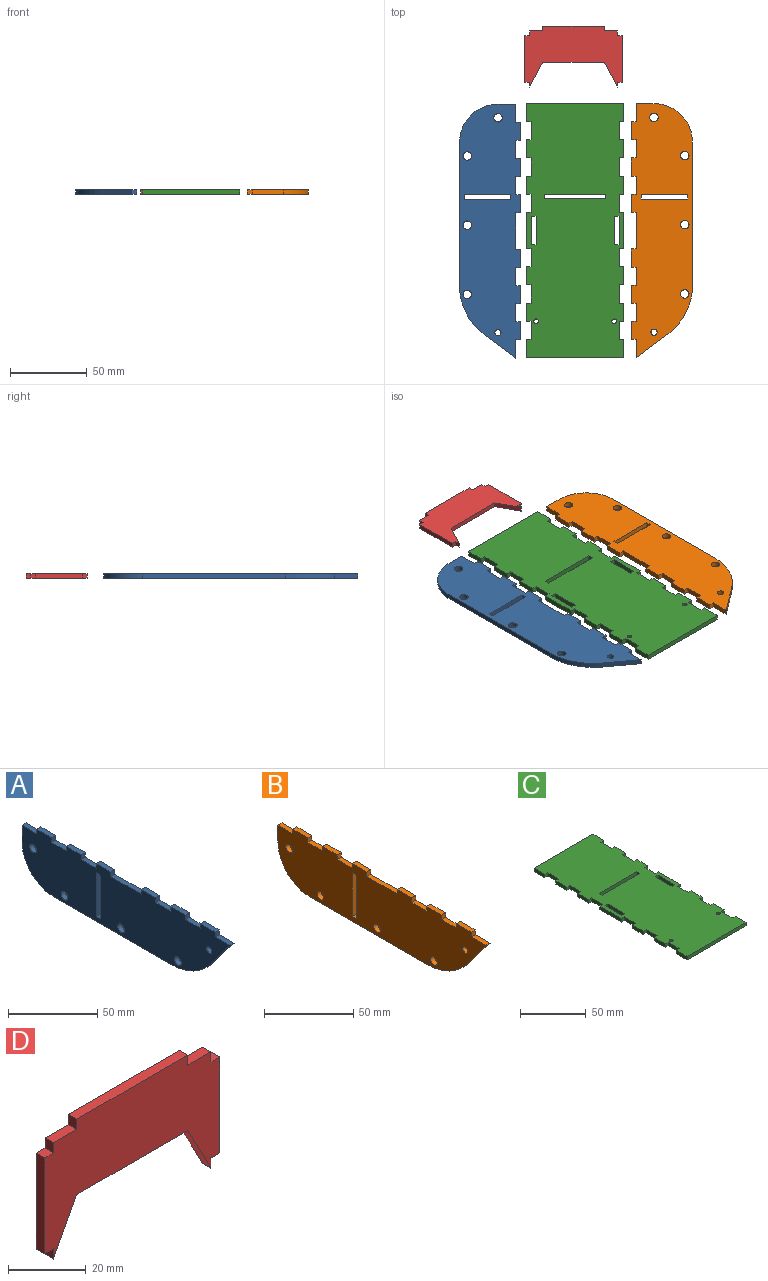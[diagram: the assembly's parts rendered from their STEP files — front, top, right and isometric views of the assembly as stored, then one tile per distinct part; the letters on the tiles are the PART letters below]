
ASSEMBLY  parts=4 mates=3
PART A: 41 faces, bbox 3.2x165.1x39.7 mm
  f0: plane 165.1x39.68mm, normal (-1,0,0), area 5359.6mm2, adj f1,f2,f3,f4,f5,f6,f7,f8
  f1: plane 11.79x3.18mm, normal (0,0,1), area 37.4mm2, adj f0,f2,f28,f29
  f2: plane 3.18x3.18mm, normal (0,-1,0), area 10.1mm2, adj f0,f1,f3,f29
  f3: plane 11.72x3.18mm, normal (0,0,1), area 37.2mm2, adj f0,f2,f4,f29
  f4: plane 3.18x3.18mm, normal (0,1,0), area 10.1mm2, adj f0,f3,f5,f29
  f5: plane 11.79x3.18mm, normal (0,0,1), area 37.4mm2, adj f0,f4,f6,f29
  f6: plane 3.18x3.18mm, normal (0,-1,0), area 10.1mm2, adj f0,f5,f7,f29
  f7: plane 11.72x3.18mm, normal (0,0,1), area 37.2mm2, adj f0,f6,f8,f29
  f8: plane 3.18x3.18mm, normal (0,1,0), area 10.1mm2, adj f0,f7,f9,f29
  f9: plane 11.79x3.18mm, normal (0,0,1), area 37.4mm2, adj f0,f8,f10,f29
  f10: plane 3.18x3.18mm, normal (0,-1,0), area 10.1mm2, adj f0,f9,f11,f29
  f11: plane 11.79x3.18mm, normal (0,0,1), area 37.4mm2, adj f0,f10,f12,f29
  f12: plane 20.51x15.27mm, normal (0,-0.8,-0.6), area 81.2mm2, adj f0,f11,f13,f29
  f13: cylinder r=39.68mm len=31.83mm, axis (1,0,0), area 117.3mm2, adj f0,f12,f14,f29
  f14: plane 93x3.18mm, normal (0,0,-1), area 295.3mm2, adj f0,f13,f15,f29
  f15: cylinder r=25mm len=25mm, axis (1,0,0), area 124.7mm2, adj f0,f14,f16,f29
  f16: plane 11.5x3.18mm, normal (0,1,0), area 36.5mm2, adj f0,f15,f17,f29
  f17: plane 11.79x3.18mm, normal (0,0,1), area 37.4mm2, adj f0,f16,f18,f29
  f18: plane 3.18x3.18mm, normal (0,1,0), area 10.1mm2, adj f0,f17,f19,f29
  f19: plane 11.79x3.18mm, normal (0,0,1), area 37.4mm2, adj f0,f18,f20,f29
  f20: plane 3.18x3.18mm, normal (0,-1,0), area 10.1mm2, adj f0,f19,f21,f29
  f21: plane 11.72x3.18mm, normal (0,0,1), area 37.2mm2, adj f0,f20,f22,f29
  f22: plane 3.18x3.18mm, normal (0,1,0), area 10.1mm2, adj f0,f21,f23,f29
  f23: plane 11.79x3.18mm, normal (0,0,1), area 37.4mm2, adj f0,f22,f24,f29
  f24: plane 3.18x3.18mm, normal (0,-1,0), area 10.1mm2, adj f0,f23,f25,f29
  f25: plane 11.72x3.18mm, normal (0,0,1), area 37.2mm2, adj f0,f24,f26,f29
  f26: plane 3.18x3.18mm, normal (0,1,0), area 10.1mm2, adj f0,f25,f27,f29
  f27: plane 11.79x3.18mm, normal (0,0,1), area 37.4mm2, adj f0,f26,f29,f31
  f28: plane 3.18x3.18mm, normal (0,1,0), area 10.1mm2, adj f0,f1,f29,f32
  f29: plane 165.1x39.68mm, normal (1,0,0), area 5359.6mm2, adj f1,f2,f3,f4,f5,f6,f7,f8
  f30: cylinder r=2.75mm len=5.5mm, axis (1,0,0), area 54.9mm2, adj f0,f29
  f31: plane 3.18x3.18mm, normal (0,-1,0), area 10.1mm2, adj f0,f27,f29,f32
  f32: plane 23.89x3.18mm, normal (0,0,1), area 75.8mm2, adj f0,f28,f29,f31
  f33: cylinder r=2.75mm len=5.5mm, axis (1,0,0), area 54.9mm2, adj f0,f29
  f34: cylinder r=2mm len=4mm, axis (1,0,0), area 39.9mm2, adj f0,f29
  f35: cylinder r=2.75mm len=5.5mm, axis (1,0,0), area 54.9mm2, adj f0,f29
  f36: cylinder r=2.75mm len=5.5mm, axis (1,0,0), area 54.9mm2, adj f0,f29
  f37: plane 30.15x3.18mm, normal (0,1,0), area 95.7mm2, adj f0,f29,f39,f40
  f38: plane 30.15x3.18mm, normal (0,-1,0), area 95.7mm2, adj f0,f29,f39,f40
  f39: plane 3.18x3.18mm, normal (0,0,-1), area 10.1mm2, adj f0,f29,f37,f38
  f40: plane 3.18x3.18mm, normal (0,0,1), area 10.1mm2, adj f0,f29,f37,f38
PART B: 41 faces, bbox 3.2x165.1x39.7 mm
  f0: plane 165.1x39.68mm, normal (1,0,0), area 5359.6mm2, adj f2,f3,f4,f5,f6,f7,f8,f9
  f1: plane 165.1x39.68mm, normal (-1,0,0), area 5359.6mm2, adj f2,f3,f4,f5,f6,f7,f8,f9
  f2: plane 11.79x3.18mm, normal (0,0,1), area 37.4mm2, adj f0,f1,f3,f29
  f3: plane 3.18x3.18mm, normal (0,-1,0), area 10.1mm2, adj f0,f1,f2,f4
  f4: plane 11.72x3.18mm, normal (0,0,1), area 37.2mm2, adj f0,f1,f3,f5
  f5: plane 3.18x3.18mm, normal (0,1,0), area 10.1mm2, adj f0,f1,f4,f6
  f6: plane 11.79x3.18mm, normal (0,0,1), area 37.4mm2, adj f0,f1,f5,f7
  f7: plane 3.18x3.18mm, normal (0,-1,0), area 10.1mm2, adj f0,f1,f6,f8
  f8: plane 11.72x3.18mm, normal (0,0,1), area 37.2mm2, adj f0,f1,f7,f9
  f9: plane 3.18x3.18mm, normal (0,1,0), area 10.1mm2, adj f0,f1,f8,f10
  f10: plane 11.79x3.18mm, normal (0,0,1), area 37.4mm2, adj f0,f1,f9,f11
  f11: plane 3.18x3.18mm, normal (0,-1,0), area 10.1mm2, adj f0,f1,f10,f12
  f12: plane 11.79x3.18mm, normal (0,0,1), area 37.4mm2, adj f0,f1,f11,f13
  f13: plane 20.51x15.27mm, normal (0,-0.8,-0.6), area 81.2mm2, adj f0,f1,f12,f14
  f14: cylinder r=39.68mm len=31.83mm, axis (-1,0,0), area 117.3mm2, adj f0,f1,f13,f15
  f15: plane 93x3.18mm, normal (0,0,-1), area 295.3mm2, adj f0,f1,f14,f16
  f16: cylinder r=25mm len=25mm, axis (-1,0,0), area 124.7mm2, adj f0,f1,f15,f17
  f17: plane 11.5x3.18mm, normal (0,1,0), area 36.5mm2, adj f0,f1,f16,f18
  f18: plane 11.79x3.18mm, normal (0,0,1), area 37.4mm2, adj f0,f1,f17,f19
  f19: plane 3.18x3.18mm, normal (0,1,0), area 10.1mm2, adj f0,f1,f18,f20
  f20: plane 11.79x3.18mm, normal (0,0,1), area 37.4mm2, adj f0,f1,f19,f21
  f21: plane 3.18x3.18mm, normal (0,-1,0), area 10.1mm2, adj f0,f1,f20,f22
  f22: plane 11.72x3.18mm, normal (0,0,1), area 37.2mm2, adj f0,f1,f21,f23
  f23: plane 3.18x3.18mm, normal (0,1,0), area 10.1mm2, adj f0,f1,f22,f24
  f24: plane 11.79x3.18mm, normal (0,0,1), area 37.4mm2, adj f0,f1,f23,f25
  f25: plane 3.18x3.18mm, normal (0,-1,0), area 10.1mm2, adj f0,f1,f24,f26
  f26: plane 11.72x3.18mm, normal (0,0,1), area 37.2mm2, adj f0,f1,f25,f27
  f27: plane 3.18x3.18mm, normal (0,1,0), area 10.1mm2, adj f0,f1,f26,f28
  f28: plane 11.79x3.18mm, normal (0,0,1), area 37.4mm2, adj f0,f1,f27,f31
  f29: plane 3.18x3.18mm, normal (0,1,0), area 10.1mm2, adj f0,f1,f2,f32
  f30: cylinder r=2.75mm len=5.5mm, axis (-1,0,0), area 54.9mm2, adj f0,f1
  f31: plane 3.18x3.18mm, normal (0,-1,0), area 10.1mm2, adj f0,f1,f28,f32
  f32: plane 23.89x3.18mm, normal (0,0,1), area 75.8mm2, adj f0,f1,f29,f31
  f33: cylinder r=2.75mm len=5.5mm, axis (-1,0,0), area 54.9mm2, adj f0,f1
  f34: cylinder r=2mm len=4mm, axis (-1,0,0), area 39.9mm2, adj f0,f1
  f35: cylinder r=2.75mm len=5.5mm, axis (-1,0,0), area 54.9mm2, adj f0,f1
  f36: cylinder r=2.75mm len=5.5mm, axis (-1,0,0), area 54.9mm2, adj f0,f1
  f37: plane 30.15x3.18mm, normal (0,1,0), area 95.7mm2, adj f0,f1,f39,f40
  f38: plane 30.15x3.18mm, normal (0,-1,0), area 95.7mm2, adj f0,f1,f39,f40
  f39: plane 3.18x3.18mm, normal (0,0,-1), area 10.1mm2, adj f0,f1,f37,f38
  f40: plane 3.18x3.18mm, normal (0,0,1), area 10.1mm2, adj f0,f1,f37,f38
PART C: 68 faces, bbox 63.5x165.1x3.2 mm
  f0: plane 165.1x63.5mm, normal (0,0,1), area 9776.6mm2, adj f2,f3,f4,f5,f6,f7,f8,f9
  f1: plane 165.1x63.5mm, normal (0,0,-1), area 9776.6mm2, adj f2,f3,f4,f5,f6,f7,f8,f9
  f2: plane 11.79x3.18mm, normal (-1,0,0), area 37.4mm2, adj f0,f1,f3,f60
  f3: plane 63.5x3.18mm, normal (0,-1,0), area 201.6mm2, adj f0,f1,f2,f4
  f4: plane 11.79x3.18mm, normal (1,0,0), area 37.4mm2, adj f0,f1,f3,f5
  f5: plane 3.18x3.18mm, normal (0,1,0), area 10.1mm2, adj f0,f1,f4,f6
  f6: plane 11.79x3.18mm, normal (1,0,0), area 37.4mm2, adj f0,f1,f5,f7
  f7: plane 3.18x3.18mm, normal (0,-1,0), area 10.1mm2, adj f0,f1,f6,f8
  f8: plane 11.79x3.18mm, normal (1,0,0), area 37.4mm2, adj f0,f1,f7,f9
  f9: plane 3.18x3.18mm, normal (0,1,0), area 10.1mm2, adj f0,f1,f8,f10
  f10: plane 11.79x3.18mm, normal (1,0,0), area 37.4mm2, adj f0,f1,f9,f11
  f11: plane 3.18x3.18mm, normal (0,-1,0), area 10.1mm2, adj f0,f1,f10,f12
  f12: plane 11.79x3.18mm, normal (1,0,0), area 37.4mm2, adj f0,f1,f11,f13
  f13: plane 3.18x3.18mm, normal (0,1,0), area 10.1mm2, adj f0,f1,f12,f14
  f14: plane 11.79x3.18mm, normal (1,0,0), area 37.4mm2, adj f0,f1,f13,f15
  f15: plane 3.18x3.18mm, normal (0,-1,0), area 10.1mm2, adj f0,f1,f14,f16
  f16: plane 23.59x3.18mm, normal (1,0,0), area 74.9mm2, adj f0,f1,f15,f17
  f17: plane 3.18x3.18mm, normal (0,1,0), area 10.1mm2, adj f0,f1,f16,f18
  f18: plane 11.79x3.18mm, normal (1,0,0), area 37.4mm2, adj f0,f1,f17,f19
  f19: plane 3.18x3.18mm, normal (0,-1,0), area 10.1mm2, adj f0,f1,f18,f20
  f20: plane 11.79x3.18mm, normal (1,0,0), area 37.4mm2, adj f0,f1,f19,f21
  f21: plane 3.18x3.18mm, normal (0,1,0), area 10.1mm2, adj f0,f1,f20,f22
  f22: plane 11.79x3.18mm, normal (1,0,0), area 37.4mm2, adj f0,f1,f21,f23
  f23: plane 3.18x3.18mm, normal (0,-1,0), area 10.1mm2, adj f0,f1,f22,f24
  f24: plane 11.79x3.18mm, normal (1,0,0), area 37.4mm2, adj f0,f1,f23,f25
  f25: plane 3.18x3.18mm, normal (0,1,0), area 10.1mm2, adj f0,f1,f24,f26
  f26: plane 11.79x3.18mm, normal (1,0,0), area 37.4mm2, adj f0,f1,f25,f27
  f27: plane 3.18x3.18mm, normal (0,-1,0), area 10.1mm2, adj f0,f1,f26,f28
  f28: plane 11.79x3.18mm, normal (1,0,0), area 37.4mm2, adj f0,f1,f27,f29
  f29: plane 63.5x3.18mm, normal (0,1,0), area 201.6mm2, adj f0,f1,f28,f30
  f30: plane 11.79x3.18mm, normal (-1,0,0), area 37.4mm2, adj f0,f1,f29,f31
  f31: plane 3.18x3.18mm, normal (0,-1,0), area 10.1mm2, adj f0,f1,f30,f32
  f32: plane 11.79x3.18mm, normal (-1,0,0), area 37.4mm2, adj f0,f1,f31,f33
  f33: plane 3.18x3.18mm, normal (0,1,0), area 10.1mm2, adj f0,f1,f32,f34
  f34: plane 11.79x3.18mm, normal (-1,0,0), area 37.4mm2, adj f0,f1,f33,f35
  f35: plane 3.18x3.18mm, normal (0,-1,0), area 10.1mm2, adj f0,f1,f34,f36
  f36: plane 11.79x3.18mm, normal (-1,0,0), area 37.4mm2, adj f0,f1,f35,f37
  f37: plane 3.18x3.18mm, normal (0,1,0), area 10.1mm2, adj f0,f1,f36,f38
  f38: plane 11.79x3.18mm, normal (-1,0,0), area 37.4mm2, adj f0,f1,f37,f39
  f39: plane 3.18x3.18mm, normal (0,-1,0), area 10.1mm2, adj f0,f1,f38,f40
  f40: plane 11.79x3.18mm, normal (-1,0,0), area 37.4mm2, adj f0,f1,f39,f41
  f41: plane 3.18x3.18mm, normal (0,1,0), area 10.1mm2, adj f0,f1,f40,f42
  f42: plane 23.59x3.18mm, normal (-1,0,0), area 74.9mm2, adj f0,f1,f41,f43
  f43: plane 3.18x3.18mm, normal (0,-1,0), area 10.1mm2, adj f0,f1,f42,f44
  f44: plane 11.79x3.18mm, normal (-1,0,0), area 37.4mm2, adj f0,f1,f43,f45
  f45: plane 3.18x3.18mm, normal (0,1,0), area 10.1mm2, adj f0,f1,f44,f46
  f46: plane 11.79x3.18mm, normal (-1,0,0), area 37.4mm2, adj f0,f1,f45,f47
  f47: plane 3.18x3.18mm, normal (0,-1,0), area 10.1mm2, adj f0,f1,f46,f48
  f48: plane 11.79x3.18mm, normal (-1,0,0), area 37.4mm2, adj f0,f1,f47,f49
  f49: plane 3.18x3.18mm, normal (0,1,0), area 10.1mm2, adj f0,f1,f48,f50
  f50: plane 11.79x3.18mm, normal (-1,0,0), area 37.4mm2, adj f0,f1,f49,f51
  f51: plane 3.18x3.18mm, normal (0,-1,0), area 10.1mm2, adj f0,f1,f50,f52
  f52: plane 11.79x3.18mm, normal (-1,0,0), area 37.4mm2, adj f0,f1,f51,f60
  f53: plane 18.29x3.18mm, normal (1,0,0), area 58.1mm2, adj f0,f1,f54,f61
  f54: plane 3.18x3.18mm, normal (0,-1,0), area 10.1mm2, adj f0,f1,f53,f55
  f55: plane 18.29x3.18mm, normal (-1,0,0), area 58.1mm2, adj f0,f1,f54,f61
  f56: plane 18.29x3.18mm, normal (1,0,0), area 58.1mm2, adj f0,f1,f57,f62
  f57: plane 3.18x3.18mm, normal (0,-1,0), area 10.1mm2, adj f0,f1,f56,f58
  f58: plane 18.29x3.18mm, normal (-1,0,0), area 58.1mm2, adj f0,f1,f57,f62
  f59: cylinder r=1.5mm len=3.18mm, axis (0,0,-1), area 29.9mm2, adj f0,f1
  f60: plane 3.18x3.18mm, normal (0,1,0), area 10.1mm2, adj f0,f1,f2,f52
  f61: plane 3.18x3.18mm, normal (0,1,0), area 10.1mm2, adj f0,f1,f53,f55
  f62: plane 3.18x3.18mm, normal (0,1,0), area 10.1mm2, adj f0,f1,f56,f58
  f63: cylinder r=1.5mm len=3.18mm, axis (0,0,-1), area 29.9mm2, adj f0,f1
  f64: plane 40.22x3.18mm, normal (0,1,0), area 127.7mm2, adj f0,f1,f66,f67
  f65: plane 40.22x3.18mm, normal (0,-1,0), area 127.7mm2, adj f0,f1,f66,f67
  f66: plane 3.18x3.18mm, normal (-1,0,0), area 10.1mm2, adj f0,f1,f64,f65
  f67: plane 3.18x3.18mm, normal (1,0,0), area 10.1mm2, adj f0,f1,f64,f65
PART D: 20 faces, bbox 63.5x3x39.7 mm
  f0: plane 63.5x39.68mm, normal (0,-1,0), area 1626.9mm2, adj f1,f2,f3,f4,f5,f6,f7,f8
  f1: plane 30.15x3.02mm, normal (1,0,0), area 91.2mm2, adj f0,f2,f16,f18
  f2: plane 3.18x3.02mm, normal (0,0,1), area 9.6mm2, adj f0,f1,f3,f16
  f3: plane 3.18x3.02mm, normal (1,0,0), area 9.6mm2, adj f0,f2,f4,f16
  f4: plane 8.47x3.02mm, normal (0,0,1), area 25.6mm2, adj f0,f3,f5,f16
  f5: plane 3.18x3.02mm, normal (1,0,0), area 9.6mm2, adj f0,f4,f6,f16
  f6: plane 40.22x3.02mm, normal (0,0,1), area 121.6mm2, adj f0,f5,f7,f16
  f7: plane 3.18x3.02mm, normal (-1,0,0), area 9.6mm2, adj f0,f6,f8,f16
  f8: plane 8.47x3.02mm, normal (0,0,1), area 25.6mm2, adj f0,f7,f9,f16
  f9: plane 3.18x3.02mm, normal (-1,0,0), area 9.6mm2, adj f0,f8,f10,f16
  f10: plane 3.18x3.02mm, normal (0,0,1), area 9.6mm2, adj f0,f9,f11,f16
  f11: plane 30.15x3.02mm, normal (-1,0,0), area 91.2mm2, adj f0,f10,f12,f16
  f12: plane 3.18x3.02mm, normal (0,0,-1), area 9.6mm2, adj f0,f11,f13,f16
  f13: plane 3.18x3.02mm, normal (-1,0,0), area 9.6mm2, adj f0,f12,f14,f16
  f14: plane 15.99x8.47mm, normal (0.88,0,-0.47), area 54.7mm2, adj f0,f13,f15,f16
  f15: plane 40.22x3.02mm, normal (0,0,-1), area 121.6mm2, adj f0,f14,f16,f17
  f16: plane 63.5x39.68mm, normal (0,1,0), area 1626.9mm2, adj f1,f2,f3,f4,f5,f6,f7,f8
  f17: plane 15.99x8.47mm, normal (-0.88,0,-0.47), area 54.7mm2, adj f0,f15,f16,f19
  f18: plane 3.18x3.02mm, normal (0,0,-1), area 9.6mm2, adj f0,f1,f16,f19
  f19: plane 3.18x3.02mm, normal (1,0,0), area 9.6mm2, adj f0,f16,f17,f18
PLACE A rot(axis=(0,1,0),90deg) t=(-21.3,-35.43,-9.22)mm
PLACE B rot(axis=(0,-1,0),90deg) t=(57.18,-35.15,-9.22)mm
PLACE C t=(17.34,-35.07,19.35)mm fixed
PLACE D rot(axis=(-1,0,0),90deg) t=(16.34,153.79,102.13)mm
MATE planar C.f0 <-> D.f0  axis (0,0,1) through (17.34,23.77,22.53)mm
MATE planar C.f0 <-> B.f0  axis (0,0,1) through (17.34,23.77,22.53)mm
MATE planar C.f0 <-> A.f0  axis (0,0,1) through (17.34,23.77,22.53)mm
